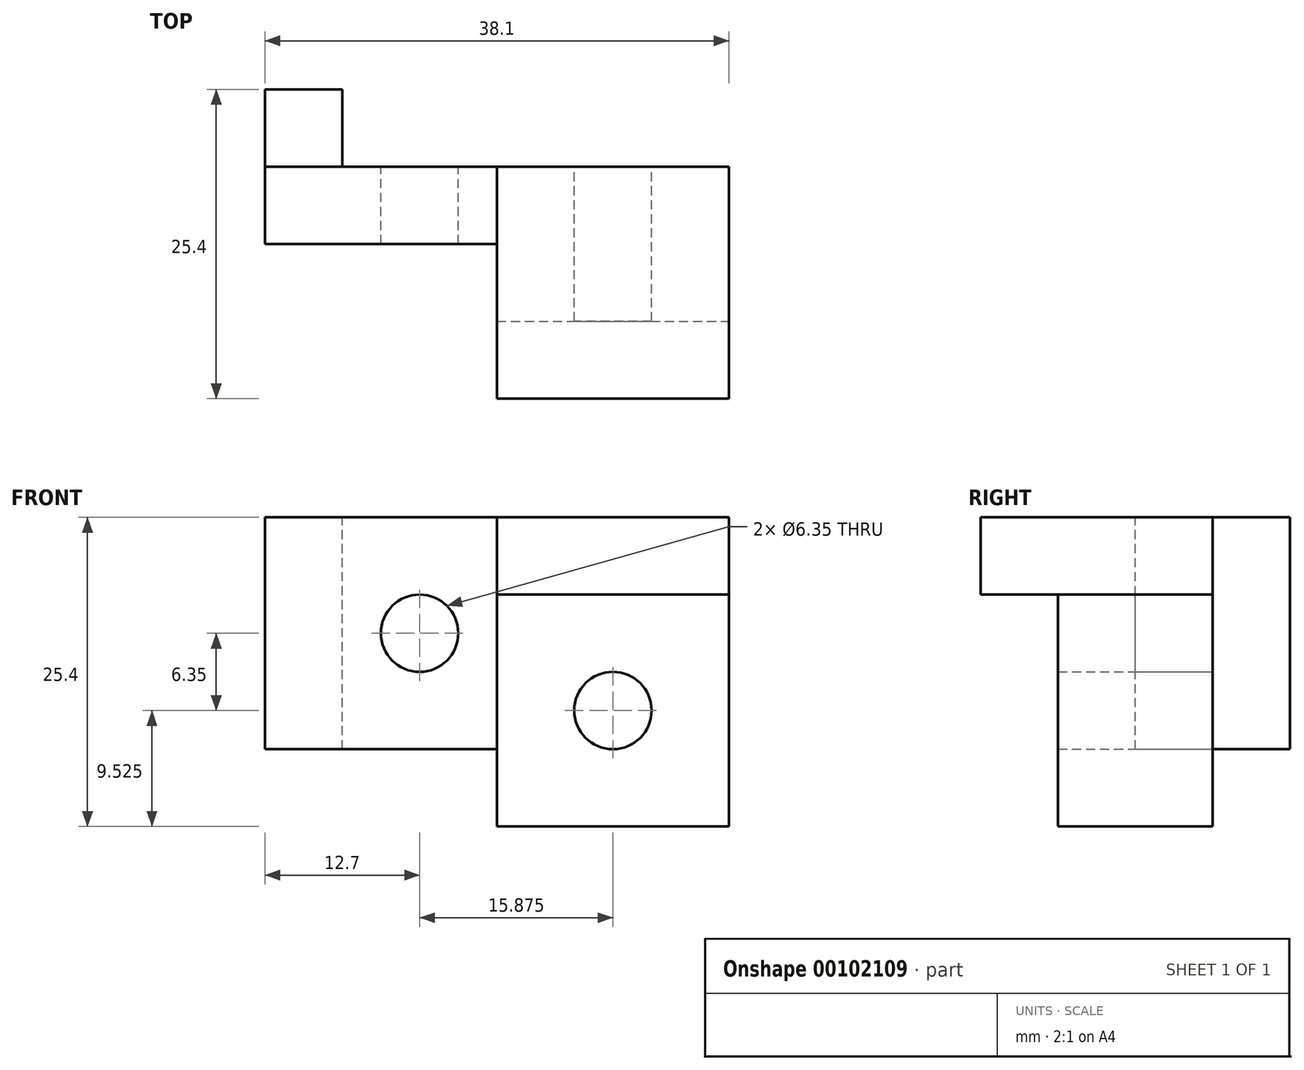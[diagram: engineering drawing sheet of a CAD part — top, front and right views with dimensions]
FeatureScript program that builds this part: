
annotation { "Feature Type Name" : "Feature", "Feature Type Description" : "" }
export const myFeature = defineFeature(function(context is Context, id is Id, definition is map)
    precondition{}
    {
        {
            var Q0;
            Q0=qCreatedBy(makeId("Front.planeOp"),FACE);
            var sketch = newSketch(context, id + "F0", { "sketchPlane" : qUnion([Q0])});
            skLineSegment(sketch, "E0.bottom", {"start": v(0, 0) * mm, "end": v(19.05, 0) * mm});
            skLineSegment(sketch, "E0.top", {"start": v(0, 19.05) * mm, "end": v(19.05, 19.05) * mm});
            skLineSegment(sketch, "E0.left", {"start": v(0, 0) * mm, "end": v(0, 19.05) * mm});
            skLineSegment(sketch, "E0.right", {"start": v(19.05, 0) * mm, "end": v(19.05, 19.05) * mm});
            skCircle(sketch, "E1", {"center": v(12.7, 9.53) * mm, "radius": 3.18 * mm});
            skSolve(sketch);
        }
        {
            var Q0;
            Q0=makeQuery(id+"F0.imprint","IMPRINT",FACE,{"disambiguationData":[TD([[makeQuery(id+"F0.imprint","IMPRINT",EDGE,{"derivedFrom":sQuery(id+"F0.wireOp",EDGE,"E0.bottom")}),1.0]])]});
            extrude(context, id + "F1", {"entities" : qUnion([Q0]), "depth" : 6.35 * mm});
        }
        {
            var Q0;
            Q0=makeQuery(id+"F0.imprint","IMPRINT",FACE,{"disambiguationData":[TD([[makeQuery(id+"F0.imprint","IMPRINT",EDGE,{"derivedFrom":sQuery(id+"F0.wireOp",EDGE,"E0.bottom")}),1.0]])]});
            var sketch = newSketch(context, id + "F2", { "sketchPlane" : qUnion([Q0])});
            skLineSegment(sketch, "E2.bottom", {"start": v(0, 0) * mm, "end": v(6.35, 0) * mm});
            skLineSegment(sketch, "E2.top", {"start": v(0, 19.05) * mm, "end": v(6.35, 19.05) * mm});
            skLineSegment(sketch, "E2.left", {"start": v(0, 0) * mm, "end": v(0, 19.05) * mm});
            skLineSegment(sketch, "E2.right", {"start": v(6.35, 0) * mm, "end": v(6.35, 19.05) * mm});
            skSolve(sketch);
        }
        {
            var Q0;
            Q0 = qSketchRegion(id + "F2", true);
            extrude(context, id + "F3", {"entities" : qUnion([Q0]), "oppositeDirection" : true, "depth" : 6.35 * mm});
        }
        {
            var Q0;
            Q0=makeQuery(id+"F1.opExtrude","CAP_FACE",FACE,{"disambiguationData":[OSD([sQuery(id+"F0.wireOp",EDGE,"E0.bottom"),sQuery(id+"F0.wireOp",EDGE,"E0.top"),sQuery(id+"F0.wireOp",EDGE,"E0.left"),sQuery(id+"F0.wireOp",EDGE,"E0.right"),sQuery(id+"F0.wireOp",EDGE,"E1")])],"isStart":false});
            var sketch = newSketch(context, id + "F4", { "sketchPlane" : qUnion([Q0])});
            skLineSegment(sketch, "E3", {"start": v(19.05, 0) * mm, "end": v(19.05, -6.35) * mm});
            skLineSegment(sketch, "E4", {"start": v(19.05, -6.35) * mm, "end": v(38.1, -6.35) * mm});
            skLineSegment(sketch, "E5", {"start": v(38.1, -6.35) * mm, "end": v(38.1, 12.7) * mm});
            skLineSegment(sketch, "E6", {"start": v(38.1, 12.7) * mm, "end": v(19.05, 12.7) * mm});
            skLineSegment(sketch, "E7", {"start": v(19.05, 12.7) * mm, "end": v(19.05, 0) * mm});
            skCircle(sketch, "E8", {"center": v(28.58, 3.18) * mm, "radius": 3.18 * mm});
            skSolve(sketch);
        }
        {
            var Q0;
            Q0 = qSketchRegion(id + "F4", true);
            extrude(context, id + "F5", {"entities" : qUnion([Q0]), "endBound" : BoundingType.SYMMETRIC, "depth" : 12.7 * mm});
        }
        {
            var Q0;
            Q0=makeQuery(id+"F1.opExtrude","CAP_FACE",FACE,{"disambiguationData":[OSD([sQuery(id+"F0.wireOp",EDGE,"E0.bottom"),sQuery(id+"F0.wireOp",EDGE,"E0.top"),sQuery(id+"F0.wireOp",EDGE,"E0.left"),sQuery(id+"F0.wireOp",EDGE,"E0.right"),sQuery(id+"F0.wireOp",EDGE,"E1")])],"isStart":true});
            var sketch = newSketch(context, id + "F6", { "sketchPlane" : qUnion([Q0])});
            skLineSegment(sketch, "E9", {"start": v(-19.05, 19.05) * mm, "end": v(-38.1, 19.05) * mm});
            skLineSegment(sketch, "E10", {"start": v(-38.1, 19.05) * mm, "end": v(-38.1, 12.7) * mm});
            skLineSegment(sketch, "E11", {"start": v(-38.1, 12.7) * mm, "end": v(-19.05, 12.7) * mm});
            skLineSegment(sketch, "E12", {"start": v(-19.05, 12.7) * mm, "end": v(-19.05, 19.05) * mm});
            skSolve(sketch);
        }
        {
            var Q0;
            Q0 = qSketchRegion(id + "F6", true);
            extrude(context, id + "F7", {"entities" : qUnion([Q0]), "oppositeDirection" : true, "depth" : 19.05 * mm});
        }
    });
